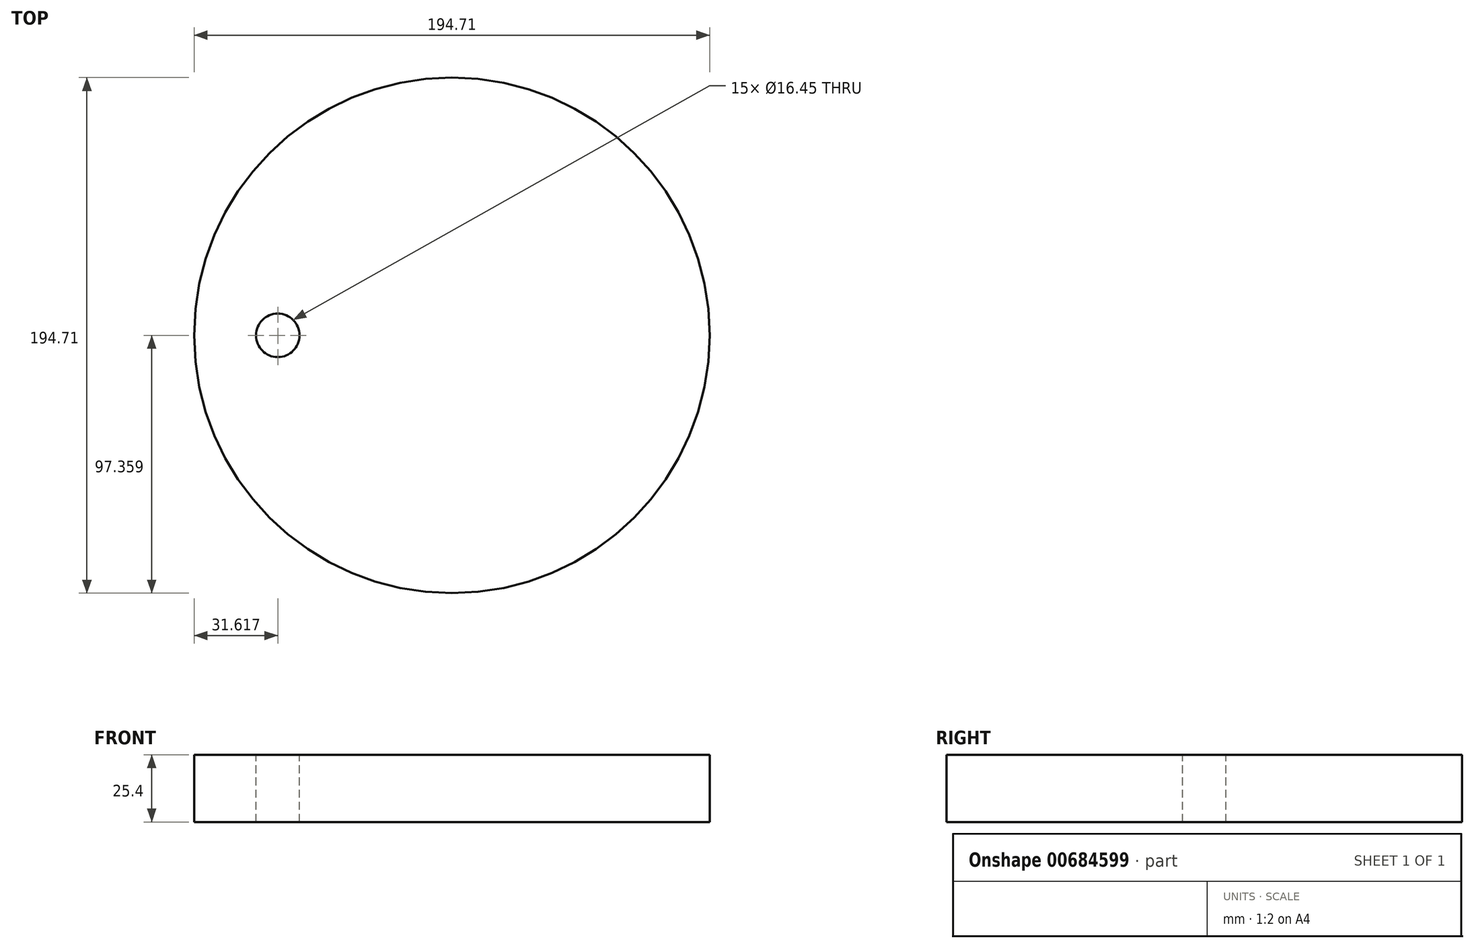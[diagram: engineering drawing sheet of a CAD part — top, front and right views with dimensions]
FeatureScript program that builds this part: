
annotation { "Feature Type Name" : "Feature", "Feature Type Description" : "" }
export const myFeature = defineFeature(function(context is Context, id is Id, definition is map)
    precondition{}
    {
        {
            var Q0;
            Q0=qCreatedBy(makeId("Top.planeOp"),FACE);
            var sketch = newSketch(context, id + "F0", { "sketchPlane" : qUnion([Q0])});
            skCircle(sketch, "E0", {"center": v(-115.5, -14.74) * mm, "radius": 97.35 * mm});
            skCircle(sketch, "E1", {"center": v(-181.23, -14.74) * mm, "radius": 8.23 * mm});
            skSolve(sketch);
        }
        {
            var Q0;
            Q0 = qSketchRegion(id + "F0", true);
            extrude(context, id + "F1", {"entities" : qUnion([Q0]), "oppositeDirection" : true, "depth" : 25.4 * mm, "offsetDistance" : 25.4 * mm});
        }
    });
